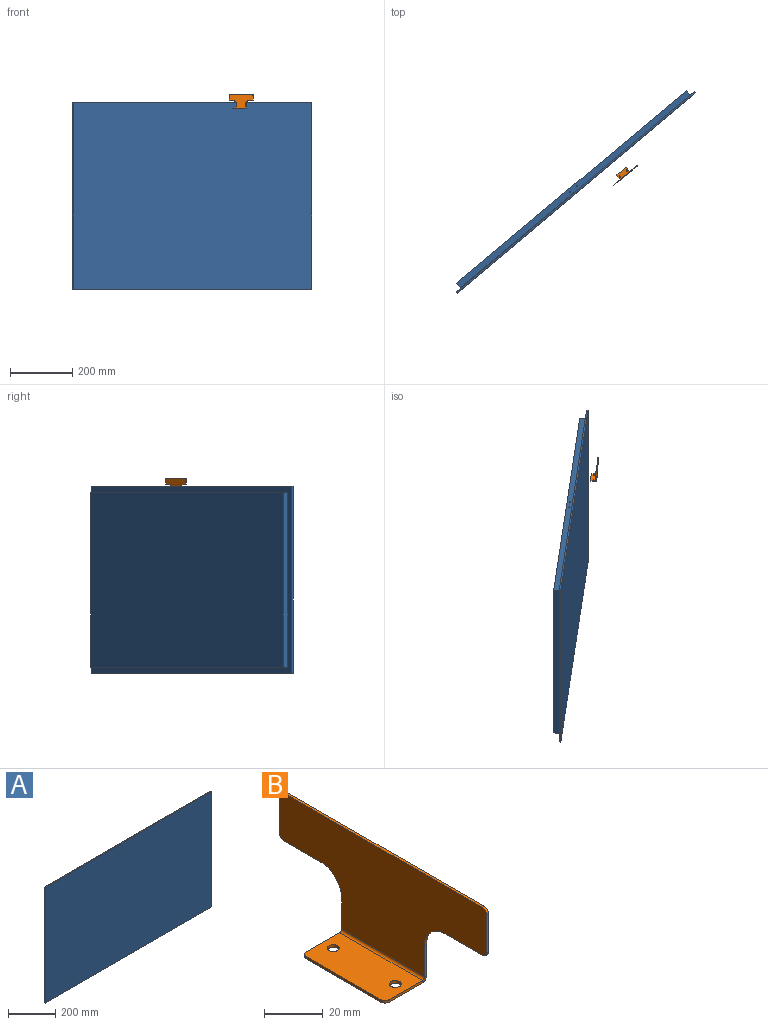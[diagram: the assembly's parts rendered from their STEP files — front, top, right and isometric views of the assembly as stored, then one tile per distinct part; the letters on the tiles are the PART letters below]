
ASSEMBLY  parts=2 mates=1
PART A: 15 faces, bbox 1000x25x600 mm
  f0: plane 1000x5mm, normal (0,0,1), area 5000mm2, adj f1,f3,f4,f5
  f1: plane 600x5mm, normal (-1,0,0), area 3000mm2, adj f0,f2,f4,f5
  f2: plane 1000x5mm, normal (0,0,-1), area 5000mm2, adj f1,f3,f4,f5
  f3: plane 600x5mm, normal (1,0,0), area 3000mm2, adj f0,f2,f4,f5
  f4: plane 1000x600mm, normal (0,-1,0), area 600000mm2, adj f0,f1,f2,f3
  f5: plane 1000x600mm, normal (0,1,0), area 62400mm2, adj f0,f1,f2,f3,f6,f7,f8,f9
  f6: plane 960x20mm, normal (0,0,1), area 19181.8mm2, adj f5,f7,f9,f10,f12,f14
  f7: plane 560x20mm, normal (1,0,0), area 11200mm2, adj f5,f6,f8,f10
  f8: plane 960x20mm, normal (0,0,-1), area 19200mm2, adj f5,f7,f9,f10
  f9: plane 560x20mm, normal (-1,0,0), area 11200mm2, adj f5,f6,f8,f10
  f10: plane 960x560mm, normal (0,1,0), area 537600mm2, adj f6,f7,f8,f9
  f11: cone r=0mm half-angle=59deg, axis (0,0,1), area 10.6mm2, adj f12
  f12: cylinder r=1.7mm len=36mm, axis (0,0,1), area 384.5mm2, adj f6,f11
  f13: cone r=0mm half-angle=59deg, axis (0,0,1), area 10.6mm2, adj f14
  f14: cylinder r=1.7mm len=36mm, axis (0,0,1), area 384.5mm2, adj f6,f13
PART B: 28 faces, bbox 20x100x45 mm
  f0: plane 16x1mm, normal (0,1,0), area 16mm2, adj f5,f6,f8,f25
  f1: plane 16x1mm, normal (0,-1,0), area 16mm2, adj f5,f6,f7,f24
  f2: cylinder r=2mm len=4mm, axis (0,0,-1), area 12.6mm2, adj f5,f6
  f3: cylinder r=2mm len=4mm, axis (0,0,-1), area 12.6mm2, adj f5,f6
  f4: plane 36x1mm, normal (-1,0,0), area 36mm2, adj f5,f6,f7,f8
  f5: plane 40x18mm, normal (0,0,-1), area 693.2mm2, adj f0,f1,f2,f3,f4,f7,f8,f26
  f6: plane 40x18mm, normal (0,0,1), area 693.2mm2, adj f0,f1,f2,f3,f4,f7,f8,f27
  f7: cylinder r=2mm len=2mm, axis (0,0,-1), area 3.1mm2, adj f1,f4,f5,f6
  f8: cylinder r=2mm len=2mm, axis (0,0,1), area 3.1mm2, adj f0,f4,f5,f6
  f9: plane 13x1mm, normal (0,1,0), area 13mm2, adj f16,f17,f23,f25
  f10: plane 18x1mm, normal (0,0,-1), area 18mm2, adj f16,f17,f18,f23
  f11: plane 16x1mm, normal (0,1,0), area 16mm2, adj f16,f17,f18,f20
  f12: plane 96x1mm, normal (0,0,1), area 96mm2, adj f16,f17,f20,f21
  f13: plane 16x1mm, normal (0,-1,0), area 16mm2, adj f16,f17,f19,f21
  f14: plane 18x1mm, normal (0,0,-1), area 18mm2, adj f16,f17,f19,f22
  f15: plane 13x1mm, normal (0,-1,0), area 13mm2, adj f16,f17,f22,f24
  f16: plane 100x43mm, normal (1,0,0), area 2959.5mm2, adj f9,f10,f11,f12,f13,f14,f15,f18
  f17: plane 100x43mm, normal (-1,0,0), area 2959.5mm2, adj f9,f10,f11,f12,f13,f14,f15,f18
  f18: cylinder r=2mm len=2mm, axis (-1,0,0), area 3.1mm2, adj f10,f11,f16,f17
  f19: cylinder r=2mm len=2mm, axis (1,0,0), area 3.1mm2, adj f13,f14,f16,f17
  f20: cylinder r=2mm len=2mm, axis (-1,0,0), area 3.1mm2, adj f11,f12,f16,f17
  f21: cylinder r=2mm len=2mm, axis (1,0,0), area 3.1mm2, adj f12,f13,f16,f17
  f22: cylinder r=10mm len=10mm, axis (1,0,0), area 15.7mm2, adj f14,f15,f16,f17
  f23: cylinder r=10mm len=10mm, axis (-1,0,0), area 15.7mm2, adj f9,f10,f16,f17
  f24: plane 2x2mm, normal (0,-1,0), area 2.4mm2, adj f1,f15,f26,f27
  f25: plane 2x2mm, normal (0,1,0), area 2.4mm2, adj f0,f9,f26,f27
  f26: cylinder r=2mm len=40mm, axis (0,-1,0), area 125.7mm2, adj f5,f16,f24,f25
  f27: cylinder r=1mm len=40mm, axis (0,-1,0), area 62.8mm2, adj f6,f17,f24,f25
PLACE A rot(axis=(0,0,1),40deg) t=(-345.35,-507.64,5.15)mm
PLACE B rot(axis=(0,0,-1),50deg) t=(-185.72,-457.24,285.15)mm
MATE planar B.f5 <-> A.f6  axis (0,0,-1) through (-192.8,-448.8,285.15)mm
